FCSTD DOCUMENT  (FreeCAD 0.15R4671 (Git))
Label: 2HEPanelBlank
License: All rights reserved
LicenseURL: http://en.wikipedia.org/wiki/All_rights_reserved
objects: Sketcher::SketchObject×1
note: 1 computed .brp shape members not serialized (recipe doc carries the construction recipe); baked Part::Feature solids carry a one-line shape summary decoded from their .brp

FEATURE [Sketcher::SketchObject] Sketch
  sketch-geometry (8):
    g0: LineSegment StartX=0 StartY=0 StartZ=0 EndX=180.083 EndY=0 EndZ=0
    g1: LineSegment StartX=180.083 StartY=0 StartZ=0 EndX=180.083 EndY=60.0749 EndZ=0
    g2: LineSegment StartX=180.083 StartY=60.0749 StartZ=0 EndX=0 EndY=60.0749 EndZ=0
    g3: LineSegment StartX=0 StartY=60.0749 StartZ=0 EndX=0 EndY=0 EndZ=0
    g4: Circle CenterX=3.70761 CenterY=56.5448 CenterZ=0 NormalX=0 NormalY=0 NormalZ=1 Radius=2.16509
    g5: Circle CenterX=3.52213 CenterY=3.96001 CenterZ=0 NormalX=0 NormalY=0 NormalZ=1 Radius=2.1986
    g6: Circle CenterX=176.579 CenterY=56.4521 CenterZ=0 NormalX=0 NormalY=0 NormalZ=1 Radius=2.22582
    g7: Circle CenterX=176.764 CenterY=3.77452 CenterZ=0 NormalX=0 NormalY=0 NormalZ=1 Radius=2.1631
  constraints (9):
    c: Coincident(g0,g1)
    c: Coincident(g1,g2)
    c: Coincident(g2,g3)
    c: Coincident(g3,g0)
    c: Horizontal(g0)
    c: Horizontal(g2)
    c: Vertical(g1)
    c: Vertical(g3)
    c: Coincident(g0,g-1)
